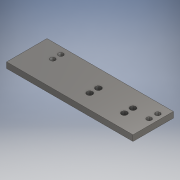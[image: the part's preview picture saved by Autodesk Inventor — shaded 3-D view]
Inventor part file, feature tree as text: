
AUTODESK INVENTOR PART (.ipt)
format: ipt  version: 2018 (Build 220112000, 112)  size: 139,264 bytes
history: native  units: mm
features: thread x4, sketch x3, hole x2, extrude x1
ambient origin geometry x8: Origin, YZ Plane, XZ Plane, XY Plane, X Axis, Y Axis, Z Axis, Center Point
bodies: Solid1 (feature_tree)
feature tree (10):
  extrude  "Extrusion1"  Depth=10.0mm
  hole  "Hole1"  [1 undecoded]
  hole  "Hole2"  [1 undecoded]
  thread  "Thread1"  [1 undecoded]
  thread  "Thread2"  [1 undecoded]
  thread  "Thread3"  [1 undecoded]
  thread  "Thread4"  [1 undecoded]
  sketch  "Sketch1"  dims[d2=10.0mm d3=0.0mm d32=32.0mm]
  sketch  "Sketch7"  dims[d34=10.0mm d36=17.0mm]
  sketch  "Sketch8"  dims[d37=10.0mm d41=36.0mm d42=12.0mm d43=14.0mm d44=8.5mm d45=6.0mm d46=4.0mm d47=2.0mm d48=90.0deg d49=0.5mm d50=20.594885mm d58=30.0mm d59=15.0mm d60=40.0mm d61=60.0mm d62=15.0mm d63=10.0mm d64=6.0mm d65=4.0mm d66=2.0mm d67=90.0deg d68=0.5mm d69=20.594885mm d70=15.0mm d71=10.0mm d72=0.0mm d73=10.0mm d74=0.0mm d75=10.0mm d76=0.0mm d77=10.0mm d78=0.0mm d81=219.0mm d82=70.0mm d83=90.0deg d84=219.0mm]
note: 6 required parameter values undecoded (feature->parameter linkage not recoverable at this tier; creation-order binding heuristic only, values carry confidence <= 0.55)
